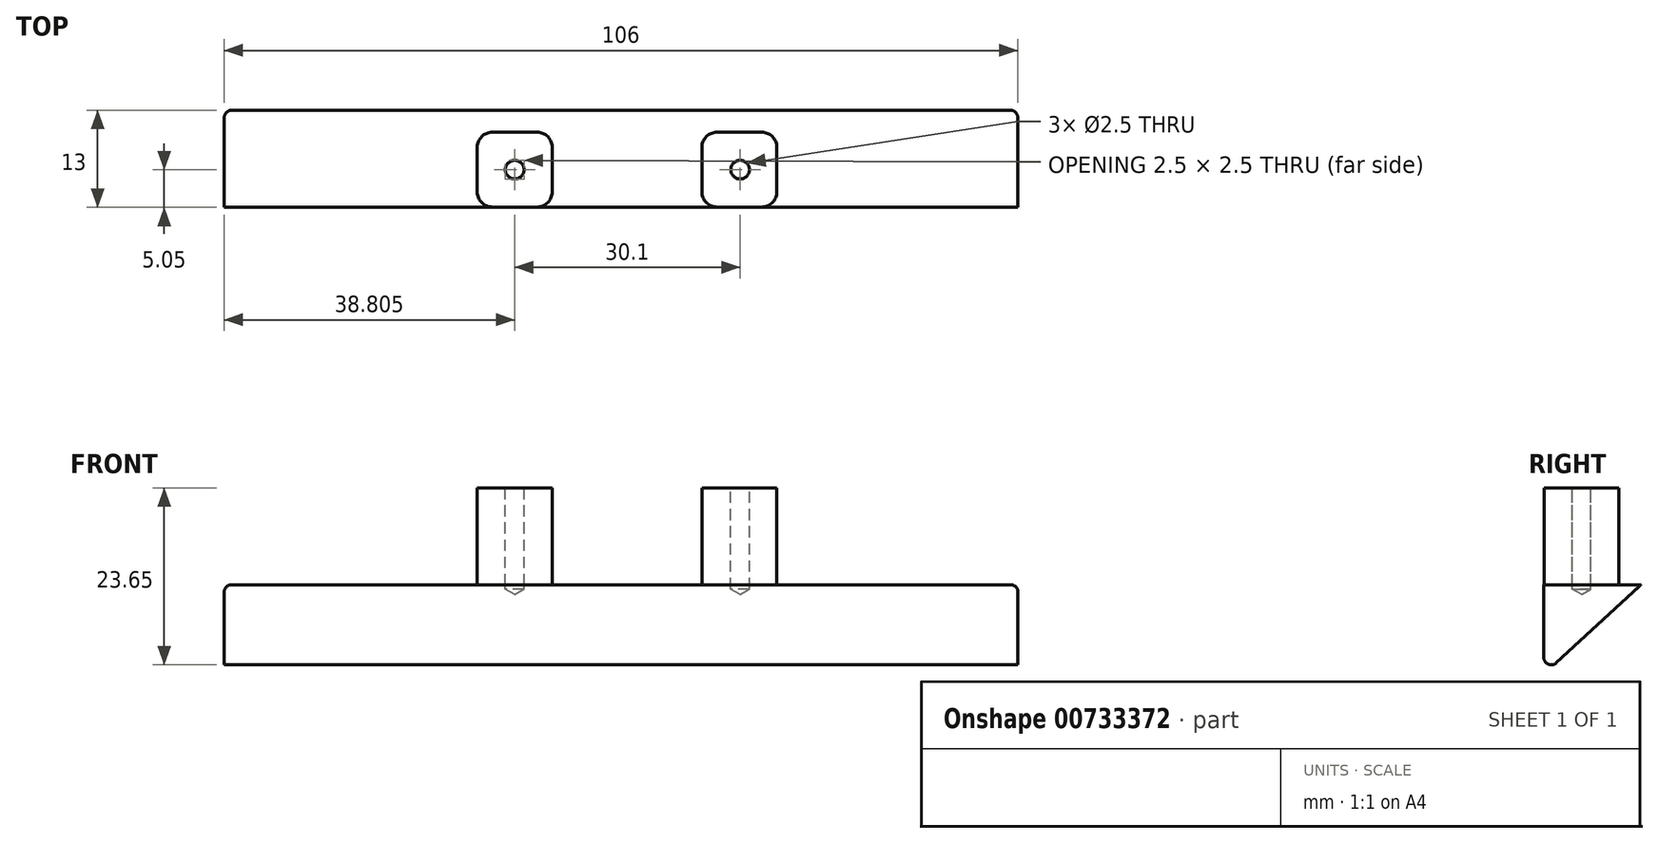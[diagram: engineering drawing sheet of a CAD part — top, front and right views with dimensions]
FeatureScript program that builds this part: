
annotation { "Feature Type Name" : "Feature", "Feature Type Description" : "" }
export const myFeature = defineFeature(function(context is Context, id is Id, definition is map)
    precondition{}
    {
        {
            var Q0;
            Q0=qCreatedBy(makeId("Right.planeOp"),FACE);
            var sketch = newSketch(context, id + "F0", { "sketchPlane" : qUnion([Q0])});
            skLineSegment(sketch, "E0", {"start": v(-5.05, 1.28) * mm, "end": v(-5.05, -10.72) * mm});
            skLineSegment(sketch, "E1", {"start": v(-5.05, 1.28) * mm, "end": v(7.95, 1.28) * mm});
            skLineSegment(sketch, "E2", {"start": v(7.95, 1.28) * mm, "end": v(-5.05, -10.72) * mm});
            skSolve(sketch);
        }
        {
            var Q0;
            Q0=makeQuery(id+"F0.imprint","IMPRINT",FACE,{"disambiguationData":[TD([[makeQuery(id+"F0.imprint","IMPRINT",EDGE,{"derivedFrom":sQuery(id+"F0.wireOp",EDGE,"E0")}),1.0]])]});
            extrude(context, id + "F1", {"entities" : qUnion([Q0]), "endBound" : BoundingType.SYMMETRIC, "depth" : 106 * mm, "offsetDistance" : 25 * mm});
        }
        {
            var Q0;
            Q0=qCreatedBy(makeId("Front.planeOp"),FACE);
            var sketch = newSketch(context, id + "F2", { "sketchPlane" : qUnion([Q0])});
            skLineSegment(sketch, "E3.bottom", {"start": v(-19.2, 14.2) * mm, "end": v(-9.2, 14.2) * mm});
            skLineSegment(sketch, "E3.top", {"start": v(-19.2, 1.2) * mm, "end": v(-9.2, 1.2) * mm});
            skLineSegment(sketch, "E3.left", {"start": v(-19.2, 14.2) * mm, "end": v(-19.2, 1.2) * mm});
            skLineSegment(sketch, "E3.right", {"start": v(-9.2, 14.2) * mm, "end": v(-9.2, 1.2) * mm});
            skLineSegment(sketch, "E4.bottom", {"start": v(10.8, 14.2) * mm, "end": v(20.8, 14.2) * mm});
            skLineSegment(sketch, "E4.top", {"start": v(10.8, 1.2) * mm, "end": v(20.8, 1.2) * mm});
            skLineSegment(sketch, "E4.left", {"start": v(10.8, 14.2) * mm, "end": v(10.8, 1.2) * mm});
            skLineSegment(sketch, "E4.right", {"start": v(20.8, 14.2) * mm, "end": v(20.8, 1.2) * mm});
            skPoint(sketch, "E5", {"position": v(-14.2, 14.2) * mm});
            skPoint(sketch, "E6", {"position": v(15.8, 14.2) * mm});
            skSolve(sketch);
        }
        {
            var Q0;
            Q0=makeQuery(id+"F2.imprint","IMPRINT",FACE,{"disambiguationData":[TD([[makeQuery(id+"F2.imprint","IMPRINT",EDGE,{"derivedFrom":sQuery(id+"F2.wireOp",EDGE,"E3.bottom")}),-1.0]])]});
            extrude(context, id + "F3", {"entities" : qUnion([Q0]), "endBound" : BoundingType.SYMMETRIC, "oppositeDirection" : true, "depth" : 10 * mm, "offsetDistance" : 25 * mm});
        }
        {
            var Q0;
            Q0=makeQuery(id+"F2.imprint","IMPRINT",FACE,{"disambiguationData":[TD([[makeQuery(id+"F2.imprint","IMPRINT",EDGE,{"derivedFrom":sQuery(id+"F2.wireOp",EDGE,"E4.bottom")}),-1.0]])]});
            extrude(context, id + "F4", {"entities" : qUnion([Q0]), "operationType" : NewBodyOperationType.ADD, "endBound" : BoundingType.SYMMETRIC, "depth" : 10 * mm, "offsetDistance" : 25 * mm});
        }
        {
            var Q0;
            Q0=makeQuery(id+"F4.opExtrude","SWEPT_FACE",FACE,{"disambiguationData":[OSD([sQuery(id+"F2.wireOp",EDGE,"E4.bottom")])]});
            var sketch = newSketch(context, id + "F5", { "sketchPlane" : qUnion([Q0])});
            skPoint(sketch, "E7", {"position": v(15.9, 0) * mm});
            skSolve(sketch);
        }
        {
            var Q0;
            Q0=makeQuery(id+"F3.opExtrude","SWEPT_FACE",FACE,{"disambiguationData":[OSD([sQuery(id+"F2.wireOp",EDGE,"E3.bottom")])]});
            var sketch = newSketch(context, id + "F6", { "sketchPlane" : qUnion([Q0])});
            skPoint(sketch, "E8", {"position": v(-14.2, 0) * mm});
            skPoint(sketch, "E8.positionSnap0", {"position": v(-14.2, -5) * mm});
            skSolve(sketch);
        }
        {
            var Q0;
            Q0=sQuery(id+"F6.wireOp",VERTEX,"E8");
            var Q1;
            Q1=sQuery(id+"F5.wireOp",VERTEX,"E7");
            var Q2;
            Q2=makeQuery(id+"F1.opExtrude","SWEPT_BODY",BODY,{"disambiguationData":[OSD([sQuery(id+"F0.wireOp",EDGE,"E0"),sQuery(id+"F0.wireOp",EDGE,"E1"),sQuery(id+"F0.wireOp",EDGE,"E2")])]});
            var Q3;
            Q3=makeQuery(id+"F3.opExtrude","SWEPT_BODY",BODY,{"disambiguationData":[OSD([sQuery(id+"F2.wireOp",EDGE,"E3.bottom"),sQuery(id+"F2.wireOp",EDGE,"E3.top"),sQuery(id+"F2.wireOp",EDGE,"E3.left"),sQuery(id+"F2.wireOp",EDGE,"E3.right")])]});
            hole(context, id + "F7", {"style" : HoleStyle.SIMPLE, "endStyle" : HoleEndStyle.BLIND, "standardTappedOrClearance" : lookupTablePath({ "standard" : "ISO", "engagement" : "75%", "pitch" : "0.5 mm", "size" : "M3", "type" : "Tapped" }), "standardBlindInLast" : lookupTablePath({ "standard" : "ISO", "engagement" : "75%", "pitch" : "0.5 mm", "size" : "M3", "type" : "Tapped" }), "holeDiameter" : 2.5 * mm, "majorDiameter" : 3 * mm, "showTappedDepth" : true, "holeDepth" : 13.5 * mm, "isTappedThrough" : true, "tappedDepth" : 12 * mm, "tapClearance" : 3, "locations" : qUnion([Q0, Q1]), "scope" : qUnion([Q2, Q3])});
        }
        {
            var Q0;
            Q0=makeQuery(id+"F3.opExtrude","CAP_EDGE",EDGE,{"disambiguationData":[OSD([sQuery(id+"F2.wireOp",EDGE,"E3.right")])],"isStart":true});
            var Q1;
            Q1=makeQuery(id+"F3.opExtrude","CAP_EDGE",EDGE,{"disambiguationData":[OSD([sQuery(id+"F2.wireOp",EDGE,"E3.right")])],"isStart":false});
            var Q2;
            Q2=makeQuery(id+"F4.opExtrude","CAP_EDGE",EDGE,{"disambiguationData":[OSD([sQuery(id+"F2.wireOp",EDGE,"E4.left")])],"isStart":false});
            var Q3;
            Q3=makeQuery(id+"F4.opExtrude","CAP_EDGE",EDGE,{"disambiguationData":[OSD([sQuery(id+"F2.wireOp",EDGE,"E4.right")])],"isStart":false});
            var Q4;
            Q4=makeQuery(id+"F4.opExtrude","CAP_EDGE",EDGE,{"disambiguationData":[OSD([sQuery(id+"F2.wireOp",EDGE,"E4.right")])],"isStart":true});
            var Q5;
            Q5=makeQuery(id+"F4.opExtrude","CAP_EDGE",EDGE,{"disambiguationData":[OSD([sQuery(id+"F2.wireOp",EDGE,"E4.left")])],"isStart":true});
            var Q6;
            Q6=makeQuery(id+"F3.opExtrude","CAP_EDGE",EDGE,{"disambiguationData":[OSD([sQuery(id+"F2.wireOp",EDGE,"E3.left")])],"isStart":false});
            var Q7;
            Q7=makeQuery(id+"F3.opExtrude","CAP_EDGE",EDGE,{"disambiguationData":[OSD([sQuery(id+"F2.wireOp",EDGE,"E3.left")])],"isStart":true});
            fillet(context, id + "F8", {"entities" : qUnion([Q0, Q1, Q2, Q3, Q4, Q5, Q6, Q7]), "radius" : 2 * mm, "tangentPropagation" : true, "allowEdgeOverflow" : false});
        }
        {
            var Q0;
            Q0=makeQuery(id+"F1.opExtrude","CAP_EDGE",EDGE,{"disambiguationData":[OSD([sQuery(id+"F0.wireOp",EDGE,"E1")])],"isStart":false});
            var Q1;
            Q1=makeQuery(id+"F1.opExtrude","CAP_EDGE",EDGE,{"disambiguationData":[OSD([sQuery(id+"F0.wireOp",EDGE,"E1")])],"isStart":true});
            var Q2;
            Q2=makeQuery(id+"F1.opExtrude","SWEPT_EDGE",EDGE,{"disambiguationData":[OSD([sQuery(id+"F0.wireOp",EDGE,"E0"),sQuery(id+"F0.wireOp",EDGE,"E2")])]});
            fillet(context, id + "F9", {"entities" : qUnion([Q0, Q1, Q2]), "radius" : 1 * mm, "tangentPropagation" : true, "allowEdgeOverflow" : false});
        }
    });
